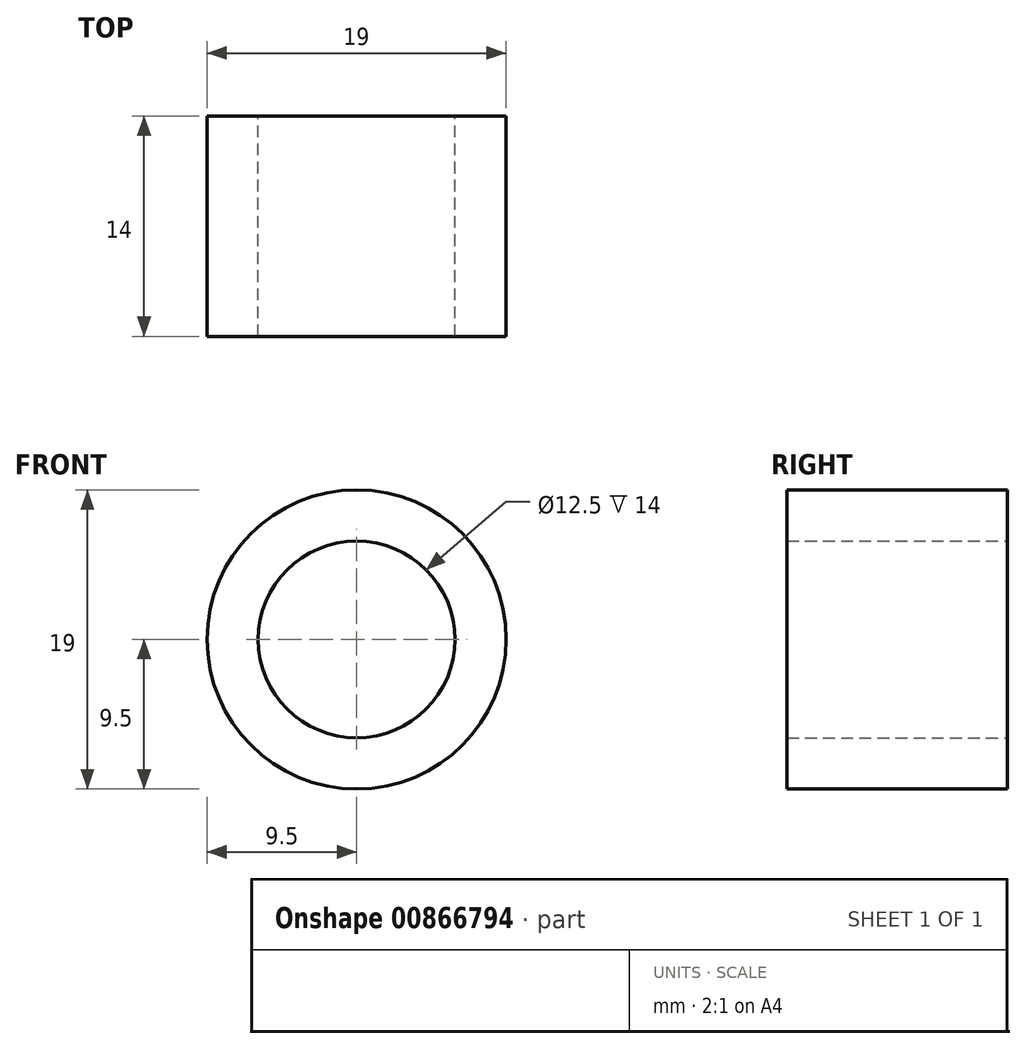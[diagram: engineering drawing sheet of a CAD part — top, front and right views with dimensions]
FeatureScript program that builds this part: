
annotation { "Feature Type Name" : "Feature", "Feature Type Description" : "" }
export const myFeature = defineFeature(function(context is Context, id is Id, definition is map)
    precondition{}
    {
        {
            var Q0;
            Q0=qCreatedBy(makeId("Front.planeOp"),FACE);
            var sketch = newSketch(context, id + "F0", { "sketchPlane" : qUnion([Q0])});
            skCircle(sketch, "E0", {"center": v(0, 0) * mm, "radius": 9.5 * mm});
            skCircle(sketch, "E1", {"center": v(0, 0) * mm, "radius": 6.25 * mm});
            skSolve(sketch);
        }
        {
            var Q0;
            Q0 = qSketchRegion(id + "F0", true);
            extrude(context, id + "F1", {"entities" : qUnion([Q0]), "depth" : 14 * mm, "offsetDistance" : 25 * mm});
        }
    });
